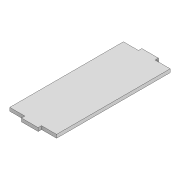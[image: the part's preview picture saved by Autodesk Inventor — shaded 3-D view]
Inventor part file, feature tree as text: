
AUTODESK INVENTOR PART (.ipt)
format: ipt  version: 2022 (Build 260153000, 153)  size: 89,088 bytes
history: native  units: mm
features: extrude x1, sketch x1
ambient origin geometry x8: Origin, YZ Plane, XZ Plane, XY Plane, X Axis, Y Axis, Z Axis, Center Point
bodies: Solid1 (feature_tree)
feature tree (2):
  extrude  "Extrusion1"  Depth=170.0mm
  sketch  "Sketch1"  dims[d0=70.0mm d1=170.0mm d2=25.0mm d3=5.0mm d4=22.5mm d5=25.0mm d6=5.0mm d7=5.0mm d8=0.0mm]
